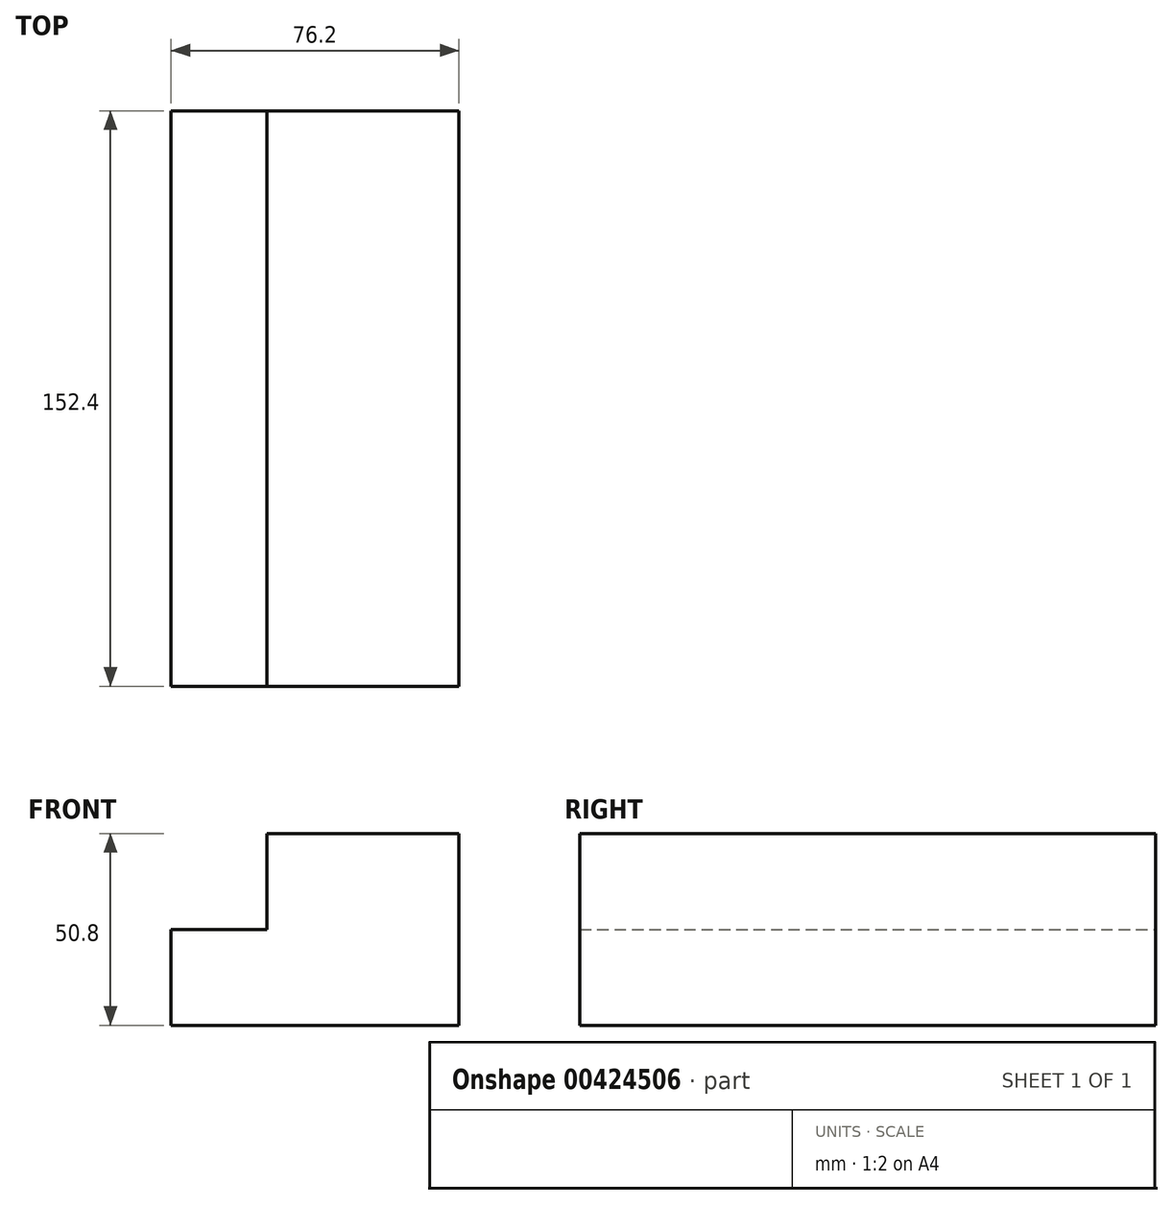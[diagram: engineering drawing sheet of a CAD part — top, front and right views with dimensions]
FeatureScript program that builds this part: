
annotation { "Feature Type Name" : "Feature", "Feature Type Description" : "" }
export const myFeature = defineFeature(function(context is Context, id is Id, definition is map)
    precondition{}
    {
        {
            var Q0;
            Q0=qCreatedBy(makeId("Front.planeOp"),FACE);
            var sketch = newSketch(context, id + "F0", { "sketchPlane" : qUnion([Q0])});
            skLineSegment(sketch, "E0", {"start": v(0, 0) * mm, "end": v(76.2, 0) * mm});
            skLineSegment(sketch, "E1", {"start": v(76.2, 0) * mm, "end": v(76.2, 50.8) * mm});
            skLineSegment(sketch, "E2", {"start": v(76.2, 50.8) * mm, "end": v(25.4, 50.8) * mm});
            skLineSegment(sketch, "E3", {"start": v(25.4, 50.8) * mm, "end": v(25.4, 25.4) * mm});
            skLineSegment(sketch, "E4", {"start": v(25.4, 25.4) * mm, "end": v(0, 25.4) * mm});
            skLineSegment(sketch, "E5", {"start": v(0, 25.4) * mm, "end": v(0, 0) * mm});
            skSolve(sketch);
        }
        {
            var Q0;
            Q0 = qSketchRegion(id + "F0", true);
            extrude(context, id + "F1", {"entities" : qUnion([Q0]), "depth" : 152.4 * mm});
        }
    });
